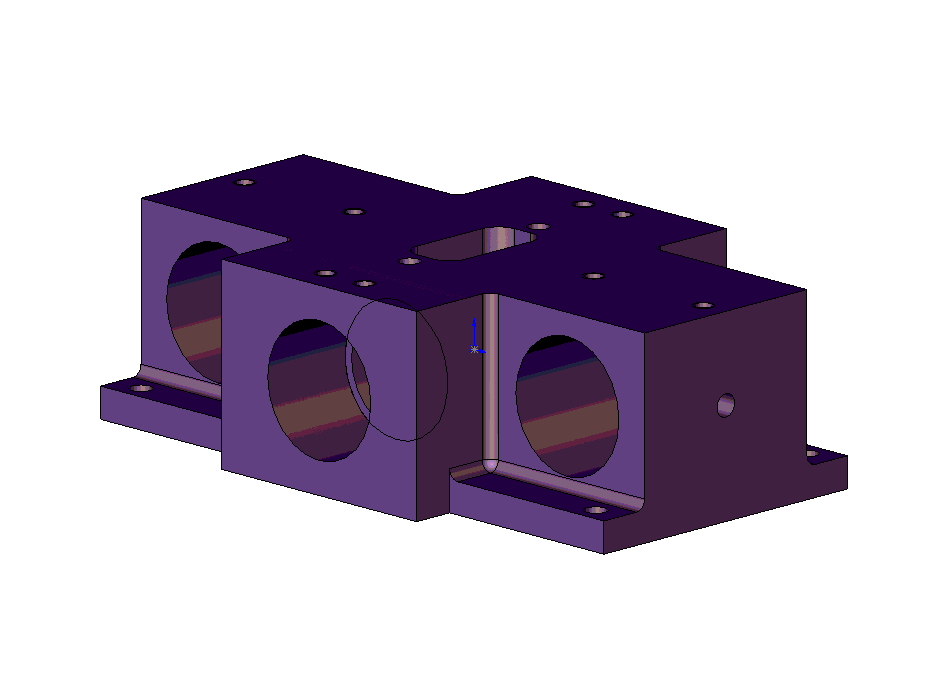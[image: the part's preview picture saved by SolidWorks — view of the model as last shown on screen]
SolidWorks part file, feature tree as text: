
SOLIDWORKS PART (.sldprt)
format: sldprt  version: not decoded by parser v0  size: 1,598,464 bytes
history: native  units: mm
features: sketch x17, thread x9, cut_extrude x6, hole x4, extrude x3, fillet x2, mirror x2, material x1 (+12 scaffold rows collapsed)
feature tree (56):
  scaffold x12  (default folders/planes/origin — collapsed)
  material  "6061 Alloy"
  sketch  "Sketch1"  dims[c1.D1=25.4mm c1.D2=48.0mm c1.D3=25.0mm c1.D4=25.0mm c2.D3=25.0mm c2.D2=20.0mm c3.D3=24.0mm c3.D4=24.0mm c3.D5=38.0mm c3.D1=48.0mm]
  extrude  "Base-Extrude"  Depth=76.2mm
  sketch  "Sketch2"  dims[c1.D1=4.1656mm c1.D2=4.9149mm c2.D1=~30.260617mm c2.D2=31.75mm]
  cut_extrude  "Grub-Screw Holes"  [1 undecoded]
  sketch  "Sketch3"  dims[D1=38.0mm D2=40.0mm]
  extrude  "Extrude1"  [1 undecoded]
  sketch  "Sketch5"  dims[D3=4.0mm D1=20.0mm D2=22.0mm]
  cut_extrude  "Access for Wire Clamp"  [1 undecoded]
  sketch  "Sketch6"  dims[D1=10.0mm]
  extrude  "Extrude3"  Depth=6mm
  fillet  "Fillet1"  Radius=2mm
  sketch  "Sketch7"  dims[D1=4.3053mm D2=4.0mm D3=6.0mm]
  cut_extrude  "Holes to Top Plate"  [1 undecoded]
  sketch  "Sketch9"  dims[D3=4.0mm D1=12.0mm D2=24.0mm]
  cut_extrude  "Access to Top Plate Bolts"  [1 undecoded]
  fillet  "Fillet2"  Radius=2mm
  sketch  "Sketch19"  dims[D1=25.4mm]
  cut_extrude  "1" Bore (Front Side)"  Depth=19.05mm
  mirror  "1" Bore (Back Side)"
  hole  "1-8 Tapped Hole1"  Diameter=22.225mm Depth=76.2mm
  sketch  "Sketch18"
  sketch  "Sketch17"  dims[hole-wizard template sketch: 59 standard entries collapsed; hole parameters kept: c18.Thru Tap Drill Dia.=22.225mm c18.Thru Tap Drill Depth=76.2mm]
  thread  "Cosmetic Thread9"  Diameter=25.4mm  [1 undecoded]
  hole  "#8-32 Tapped Hole1"  Diameter=3.4544mm Depth=8.9624mm
  sketch  "Sketch13"  dims[D1=27.0mm D2=5.5mm D3=27.0mm D4=5.5mm]
  sketch  "Sketch12"  dims[hole-wizard template sketch: 47 standard entries collapsed; hole parameters kept: c15.Tap Drill Depth=8.9624mm c15.D3=~14.816244mm c15.Drill Angle=118.0deg]
  thread  "Cosmetic Thread1"  Diameter=5mm  [1 undecoded]
  thread  "Cosmetic Thread2"  Diameter=5mm  [1 undecoded]
  thread  "Cosmetic Thread3"  Diameter=5mm  [1 undecoded]
  thread  "Cosmetic Thread4"  Diameter=5mm  [1 undecoded]
  hole  "#8-32 Tapped Hole2"  [1 undecoded]
  sketch  "Sketch15"  dims[D1=9.525mm D2=6.35mm]
  thread  "Cosmetic Thread5"  Diameter=8.083325mm  [1 undecoded]
  thread  "Cosmetic Thread6"  Diameter=8.083325mm  [1 undecoded]
  thread  "Cosmetic Thread7"  Diameter=8.083325mm  [1 undecoded]
  thread  "Cosmetic Thread8"  Diameter=8.083325mm  [1 undecoded]
  sketch  "Sketch14"  dims[hole-wizard template sketch: 60 standard entries collapsed; hole parameters kept: c18.Thru Tap Drill Depth=~7.226785mm]
  sketch  "Sketch22"  dims[c1.D1=25.4mm c1.D3=25.4mm c1.D2=21.0mm c2.D3=19.0mm]
  cut_extrude  "Holes for Added Mass"  [1 undecoded]
  hole  "#8 Clearance Hole1"  Diameter=4.3053mm Depth=51.068959mm
  sketch  "Sketch24"  dims[D1=21.0mm D2=~2.002053mm]
  sketch  "Sketch23"  dims[hole-wizard template sketch: 60 standard entries collapsed; hole parameters kept: c18.Thru Hole Depth=~51.068959mm]
  mirror  "Mirror1"
decode coverage: 33 of 43 modeling features carry decoded parameters
note: ~ marks probable driven/reference dimensions
note: 16 parameter values undecoded
summary: no parameter record found for 7 features
note: suppression state not decoded; provenance and decode notes live in map.json
